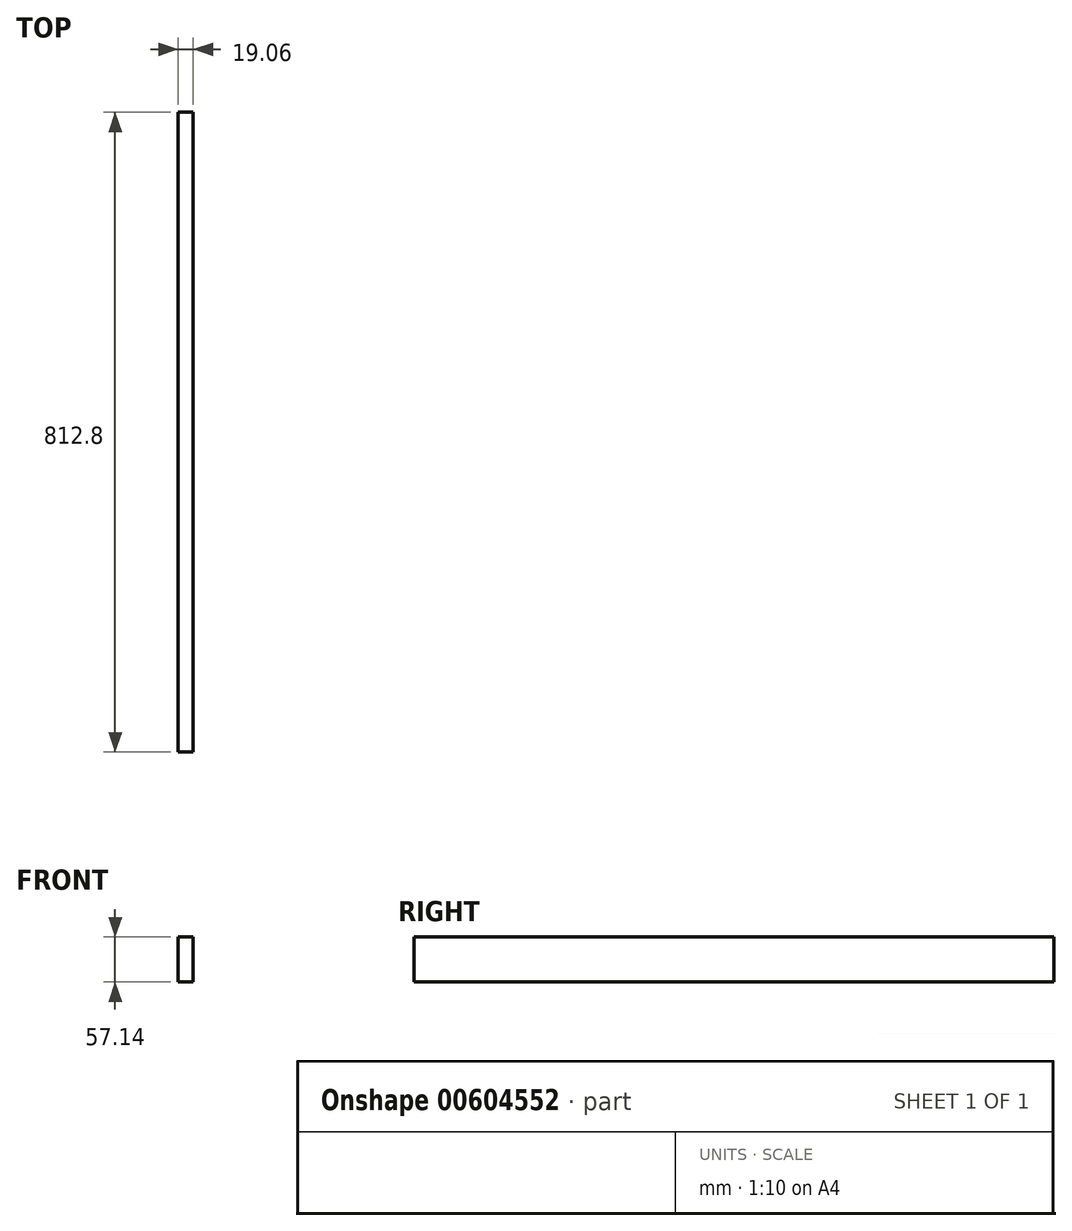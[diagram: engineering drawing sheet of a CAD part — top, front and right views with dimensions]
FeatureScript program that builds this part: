
annotation { "Feature Type Name" : "Feature", "Feature Type Description" : "" }
export const myFeature = defineFeature(function(context is Context, id is Id, definition is map)
    precondition{}
    {
        {
            var Q0;
            Q0=qCreatedBy(makeId("Front.planeOp"),FACE);
            var sketch = newSketch(context, id + "F0", { "sketchPlane" : qUnion([Q0])});
            skLineSegment(sketch, "E0.bottom", {"start": v(9.52, -28.58) * mm, "end": v(-9.53, -28.58) * mm});
            skLineSegment(sketch, "E0.top", {"start": v(9.53, 28.58) * mm, "end": v(-9.52, 28.58) * mm});
            skLineSegment(sketch, "E0.left", {"start": v(9.52, -28.58) * mm, "end": v(9.53, 28.58) * mm});
            skLineSegment(sketch, "E0.right", {"start": v(-9.53, -28.58) * mm, "end": v(-9.52, 28.58) * mm});
            skPoint(sketch, "E0.middle", {"position": v(0, 0) * mm});
            skSolve(sketch);
        }
        {
            var Q0;
            Q0=makeQuery(id+"F0.imprint","IMPRINT",FACE,{"disambiguationData":[TD([[makeQuery(id+"F0.imprint","IMPRINT",EDGE,{"derivedFrom":sQuery(id+"F0.wireOp",EDGE,"E0.bottom")}),-1.0]])]});
            extrude(context, id + "F1", {"entities" : qUnion([Q0]), "depth" : 812.8 * mm});
        }
    });
